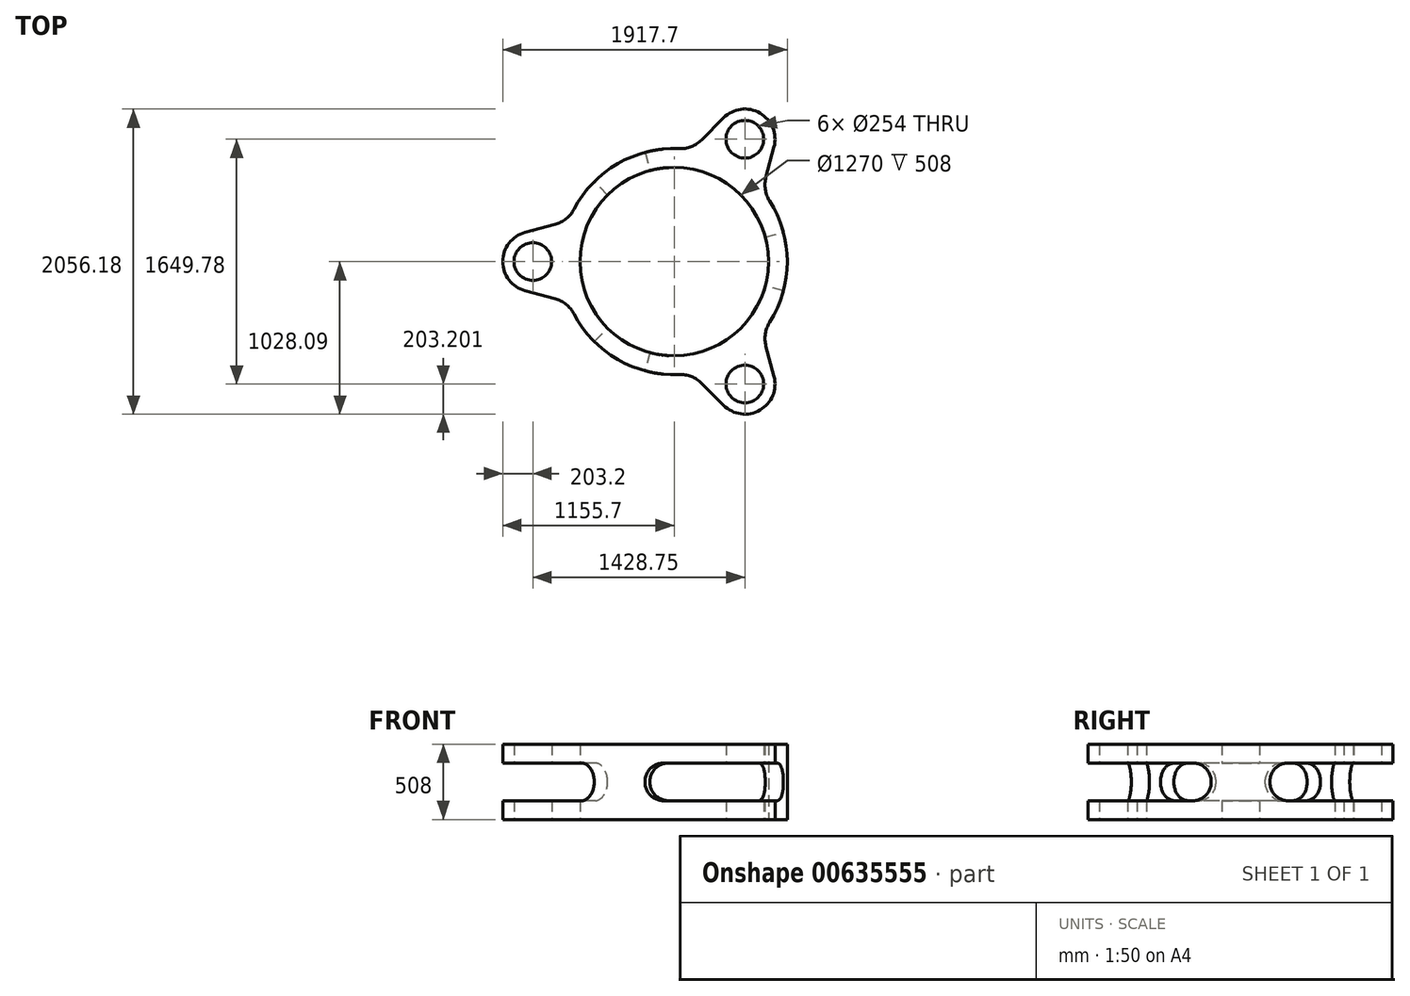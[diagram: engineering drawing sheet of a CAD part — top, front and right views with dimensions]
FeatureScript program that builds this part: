
annotation { "Feature Type Name" : "Feature", "Feature Type Description" : "" }
export const myFeature = defineFeature(function(context is Context, id is Id, definition is map)
    precondition{}
    {
        {
            var Q0;
            Q0=qCreatedBy(makeId("Top.planeOp"),FACE);
            var sketch = newSketch(context, id + "F0", { "sketchPlane" : qUnion([Q0])});
            skArc(sketch, "E0", {"start": v(-675.48, -352.66) * mm, "mid": v(762, 0) * mm, "end": v(-675.48, 352.66) * mm});
            skCircle(sketch, "E1", {"center": v(-952.5, 0) * mm, "radius": 127 * mm});
            skCircle(sketch, "E2", {"center": v(0, 0) * mm, "radius": 635 * mm});
            skArc(sketch, "E3", {"start": v(-1005.1, 196.28) * mm, "mid": v(-1155.7, 0) * mm, "end": v(-1005.1, -196.28) * mm});
            skLineSegment(sketch, "E4", {"start": v(-1005.1, 196.28) * mm, "end": v(-803.02, 250.42) * mm});
            skLineSegment(sketch, "E5", {"start": v(-952.5, 0) * mm, "end": v(0, 0) * mm, "construction": true});
            skLineSegment(sketch, "E6.MirrorCS", {"start": v(-1005.1, -196.28) * mm, "end": v(-803.02, -250.42) * mm});
            skCircle(sketch, "E7", {"center": v(0, 0) * mm, "radius": 952.5 * mm, "construction": true});
            skPoint(sketch, "E8.visualSharp", {"position": v(-710.57, 275.2) * mm});
            skArc(sketch, "E8.filletArc", {"start": v(-803.02, 250.42) * mm, "mid": v(-728.52, 288.15) * mm, "end": v(-675.48, 352.66) * mm});
            skPoint(sketch, "E9.visualSharp", {"position": v(-710.57, -275.2) * mm});
            skArc(sketch, "E9.filletArc", {"start": v(-675.48, -352.66) * mm, "mid": v(-728.52, -288.15) * mm, "end": v(-803.02, -250.42) * mm});
            skArc(sketch, "E10.1.0", {"start": v(184.64, -820.65) * mm, "mid": v(114.72, -775) * mm, "end": v(32.33, -761.31) * mm});
            skLineSegment(sketch, "E10.1.1", {"start": v(332.57, -968.57) * mm, "end": v(184.64, -820.65) * mm});
            skArc(sketch, "E10.1.2", {"start": v(332.57, -968.57) * mm, "mid": v(577.85, -1000.87) * mm, "end": v(672.53, -772.3) * mm});
            skLineSegment(sketch, "E10.1.3", {"start": v(672.53, -772.3) * mm, "end": v(618.38, -570.23) * mm});
            skArc(sketch, "E10.1.4", {"start": v(643.15, -408.66) * mm, "mid": v(613.8, -486.84) * mm, "end": v(618.38, -570.23) * mm});
            skArc(sketch, "E10.2.0", {"start": v(618.38, 570.23) * mm, "mid": v(613.8, 486.84) * mm, "end": v(643.15, 408.66) * mm});
            skLineSegment(sketch, "E10.2.1", {"start": v(672.53, 772.3) * mm, "end": v(618.38, 570.23) * mm});
            skArc(sketch, "E10.2.2", {"start": v(672.53, 772.3) * mm, "mid": v(577.85, 1000.87) * mm, "end": v(332.57, 968.57) * mm});
            skLineSegment(sketch, "E10.2.3", {"start": v(332.57, 968.57) * mm, "end": v(184.64, 820.65) * mm});
            skArc(sketch, "E10.2.4", {"start": v(32.33, 761.31) * mm, "mid": v(114.72, 775) * mm, "end": v(184.64, 820.65) * mm});
            skCircle(sketch, "E11.1.0", {"center": v(476.25, -824.89) * mm, "radius": 127 * mm});
            skCircle(sketch, "E11.2.0", {"center": v(476.25, 824.89) * mm, "radius": 127 * mm});
            skSolve(sketch);
        }
        {
            var Q0;
            Q0 = qSketchRegion(id + "F0", true);
            extrude(context, id + "F1", {"entities" : qUnion([Q0]), "endBound" : BoundingType.SYMMETRIC, "depth" : 508 * mm, "offsetDistance" : 25.4 * mm});
        }
        {
            var Q0;
            Q0=qCreatedBy(makeId("Top.planeOp"),FACE);
            var sketch = newSketch(context, id + "F2", { "sketchPlane" : qUnion([Q0])});
            skArc(sketch, "E12.0.0", {"start": v(618.38, -570.23) * mm, "mid": v(613.8, -486.84) * mm, "end": v(643.15, -408.66) * mm});
            skArc(sketch, "E12.0.1", {"start": v(643.15, -408.66) * mm, "mid": v(697.65, -306.48) * mm, "end": v(736.04, -197.22) * mm});
            skArc(sketch, "E12.0.2", {"start": v(643.15, 408.66) * mm, "mid": v(613.8, 486.84) * mm, "end": v(618.38, 570.23) * mm});
            skLineSegment(sketch, "E12.0.3", {"start": v(618.38, 570.23) * mm, "end": v(672.53, 772.3) * mm});
            skArc(sketch, "E12.0.4", {"start": v(672.53, 772.3) * mm, "mid": v(577.85, 1000.87) * mm, "end": v(332.57, 968.57) * mm});
            skLineSegment(sketch, "E12.0.5", {"start": v(332.57, 968.57) * mm, "end": v(184.64, 820.65) * mm});
            skArc(sketch, "E12.0.6", {"start": v(184.64, 820.65) * mm, "mid": v(114.72, 775) * mm, "end": v(32.33, 761.31) * mm});
            skArc(sketch, "E12.0.7", {"start": v(32.33, 761.31) * mm, "mid": v(-83.4, 757.42) * mm, "end": v(-197.22, 736.04) * mm});
            skArc(sketch, "E12.0.8", {"start": v(-675.48, 352.66) * mm, "mid": v(-728.52, 288.15) * mm, "end": v(-803.02, 250.42) * mm});
            skLineSegment(sketch, "E12.0.9", {"start": v(-803.02, 250.42) * mm, "end": v(-1005.1, 196.28) * mm});
            skArc(sketch, "E12.0.10", {"start": v(-1005.1, 196.28) * mm, "mid": v(-1155.7, 0) * mm, "end": v(-1005.1, -196.28) * mm});
            skLineSegment(sketch, "E12.0.11", {"start": v(-1005.1, -196.28) * mm, "end": v(-803.02, -250.42) * mm});
            skArc(sketch, "E12.0.12", {"start": v(-803.02, -250.42) * mm, "mid": v(-728.52, -288.15) * mm, "end": v(-675.48, -352.66) * mm});
            skArc(sketch, "E12.0.13", {"start": v(-675.48, -352.66) * mm, "mid": v(-614.24, -450.94) * mm, "end": v(-538.82, -538.82) * mm});
            skArc(sketch, "E12.0.14", {"start": v(32.33, -761.31) * mm, "mid": v(114.72, -775) * mm, "end": v(184.64, -820.65) * mm});
            skLineSegment(sketch, "E12.0.15", {"start": v(184.64, -820.65) * mm, "end": v(332.57, -968.57) * mm});
            skArc(sketch, "E12.0.16", {"start": v(332.57, -968.57) * mm, "mid": v(577.85, -1000.87) * mm, "end": v(672.53, -772.3) * mm});
            skLineSegment(sketch, "E12.0.17", {"start": v(672.53, -772.3) * mm, "end": v(618.38, -570.23) * mm});
            skArc(sketch, "E13.0", {"start": v(-449.01, 449.01) * mm, "mid": v(-635, 0) * mm, "end": v(-449.01, -449.01) * mm});
            skLineSegment(sketch, "E14", {"start": v(0, 0) * mm, "end": v(-952.5, 0) * mm, "construction": true});
            skLineSegment(sketch, "E15", {"start": v(0, 0) * mm, "end": v(-538.82, 538.82) * mm});
            skLineSegment(sketch, "E16", {"start": v(0, 0) * mm, "end": v(-197.22, 736.04) * mm});
            skLineSegment(sketch, "E17.1.0", {"start": v(0, 0) * mm, "end": v(-538.82, -538.82) * mm});
            skLineSegment(sketch, "E17.1.1", {"start": v(0, 0) * mm, "end": v(-197.22, -736.04) * mm});
            skLineSegment(sketch, "E17.2.0", {"start": v(0, 0) * mm, "end": v(736.04, -197.22) * mm});
            skLineSegment(sketch, "E17.2.1", {"start": v(0, 0) * mm, "end": v(736.04, 197.22) * mm});
            skArc(sketch, "E18.trimOffspring", {"start": v(-538.82, 538.82) * mm, "mid": v(-614.24, 450.94) * mm, "end": v(-675.48, 352.66) * mm});
            skArc(sketch, "E19.trimOffspring", {"start": v(736.04, 197.22) * mm, "mid": v(697.65, 306.48) * mm, "end": v(643.15, 408.66) * mm});
            skArc(sketch, "E20.trimOffspring", {"start": v(613.36, 164.35) * mm, "mid": v(317.5, 549.93) * mm, "end": v(-164.35, 613.36) * mm});
            skArc(sketch, "E21.trimOffspring", {"start": v(-197.22, -736.04) * mm, "mid": v(-83.4, -757.42) * mm, "end": v(32.33, -761.31) * mm});
            skArc(sketch, "E22.trimOffspring", {"start": v(-164.35, -613.36) * mm, "mid": v(317.5, -549.93) * mm, "end": v(613.36, -164.35) * mm});
            skSolve(sketch);
        }
        {
            var Q0;
            Q0 = qSketchRegion(id + "F2", true);
            extrude(context, id + "F3", {"entities" : qUnion([Q0]), "operationType" : NewBodyOperationType.REMOVE, "endBound" : BoundingType.SYMMETRIC, "oppositeDirection" : true, "depth" : 254 * mm, "offsetDistance" : 25.4 * mm});
        }
        {
            var Q0;
            Q0=makeQuery(id+"F3.boolean.opBoolean","COPY",EDGE,{"derivedFrom":makeQuery(id+"F3.opExtrude","CAP_EDGE",EDGE,{"disambiguationData":[OSD([sQuery(id+"F2.wireOp",EDGE,"E16")])],"isStart":false})});
            var Q1;
            Q1=makeQuery(id+"F3.boolean.opBoolean","COPY",EDGE,{"derivedFrom":makeQuery(id+"F3.opExtrude","CAP_EDGE",EDGE,{"disambiguationData":[OSD([sQuery(id+"F2.wireOp",EDGE,"E16")])],"isStart":true})});
            var Q2;
            Q2=makeQuery(id+"F3.boolean.opBoolean","COPY",EDGE,{"derivedFrom":makeQuery(id+"F3.opExtrude","CAP_EDGE",EDGE,{"disambiguationData":[OSD([sQuery(id+"F2.wireOp",EDGE,"E15")])],"isStart":false})});
            var Q3;
            Q3=makeQuery(id+"F3.boolean.opBoolean","COPY",EDGE,{"derivedFrom":makeQuery(id+"F3.opExtrude","CAP_EDGE",EDGE,{"disambiguationData":[OSD([sQuery(id+"F2.wireOp",EDGE,"E15")])],"isStart":true})});
            var Q4;
            Q4=makeQuery(id+"F3.boolean.opBoolean","COPY",EDGE,{"derivedFrom":makeQuery(id+"F3.opExtrude","CAP_EDGE",EDGE,{"disambiguationData":[OSD([sQuery(id+"F2.wireOp",EDGE,"E17.1.0")])],"isStart":false})});
            var Q5;
            Q5=makeQuery(id+"F3.boolean.opBoolean","COPY",EDGE,{"derivedFrom":makeQuery(id+"F3.opExtrude","CAP_EDGE",EDGE,{"disambiguationData":[OSD([sQuery(id+"F2.wireOp",EDGE,"E17.1.0")])],"isStart":true})});
            var Q6;
            Q6=makeQuery(id+"F3.boolean.opBoolean","COPY",EDGE,{"derivedFrom":makeQuery(id+"F3.opExtrude","CAP_EDGE",EDGE,{"disambiguationData":[OSD([sQuery(id+"F2.wireOp",EDGE,"E17.1.1")])],"isStart":false})});
            var Q7;
            Q7=makeQuery(id+"F3.boolean.opBoolean","COPY",EDGE,{"derivedFrom":makeQuery(id+"F3.opExtrude","CAP_EDGE",EDGE,{"disambiguationData":[OSD([sQuery(id+"F2.wireOp",EDGE,"E17.1.1")])],"isStart":true})});
            var Q8;
            Q8=makeQuery(id+"F3.boolean.opBoolean","COPY",EDGE,{"derivedFrom":makeQuery(id+"F3.opExtrude","CAP_EDGE",EDGE,{"disambiguationData":[OSD([sQuery(id+"F2.wireOp",EDGE,"E17.2.0")])],"isStart":false})});
            var Q9;
            Q9=makeQuery(id+"F3.boolean.opBoolean","COPY",EDGE,{"derivedFrom":makeQuery(id+"F3.opExtrude","CAP_EDGE",EDGE,{"disambiguationData":[OSD([sQuery(id+"F2.wireOp",EDGE,"E17.2.0")])],"isStart":true})});
            var Q10;
            Q10=makeQuery(id+"F3.boolean.opBoolean","COPY",EDGE,{"derivedFrom":makeQuery(id+"F3.opExtrude","CAP_EDGE",EDGE,{"disambiguationData":[OSD([sQuery(id+"F2.wireOp",EDGE,"E17.2.1")])],"isStart":false})});
            var Q11;
            Q11=makeQuery(id+"F3.boolean.opBoolean","COPY",EDGE,{"derivedFrom":makeQuery(id+"F3.opExtrude","CAP_EDGE",EDGE,{"disambiguationData":[OSD([sQuery(id+"F2.wireOp",EDGE,"E17.2.1")])],"isStart":true})});
            fillet(context, id + "F4", {"entities" : qUnion([Q0, Q1, Q2, Q3, Q4, Q5, Q6, Q7, Q8, Q9, Q10, Q11]), "radius" : 127 * mm, "tangentPropagation" : true, "allowEdgeOverflow" : false});
        }
    });
